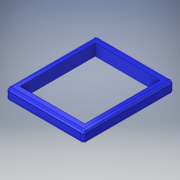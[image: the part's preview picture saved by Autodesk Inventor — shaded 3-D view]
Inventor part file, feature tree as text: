
AUTODESK INVENTOR PART (.ipt)
format: ipt  version: 2017 SP1 (Build 210196100, 196)  size: 126,464 bytes
history: native  units: in
note: dims shown in document units (in); Inventor stores cm internally (conversion verified against a paired STEP export)
features: extrude x1, fillet x1, sketch x1
ambient origin geometry x8: Origin, YZ Plane, XZ Plane, XY Plane, X Axis, Y Axis, Z Axis, Center Point
bodies: Solid1 (feature_tree)
feature tree (3):
  extrude  "Extrusion1"  Depth=28.0in
  fillet  "Fillet1"  Radius=3.25in
  sketch  "Sketch1"  dims[d0=32.5in d1=28.0in d2=3.25in d3=5.0in d4=0.0in d5=1.25in]
